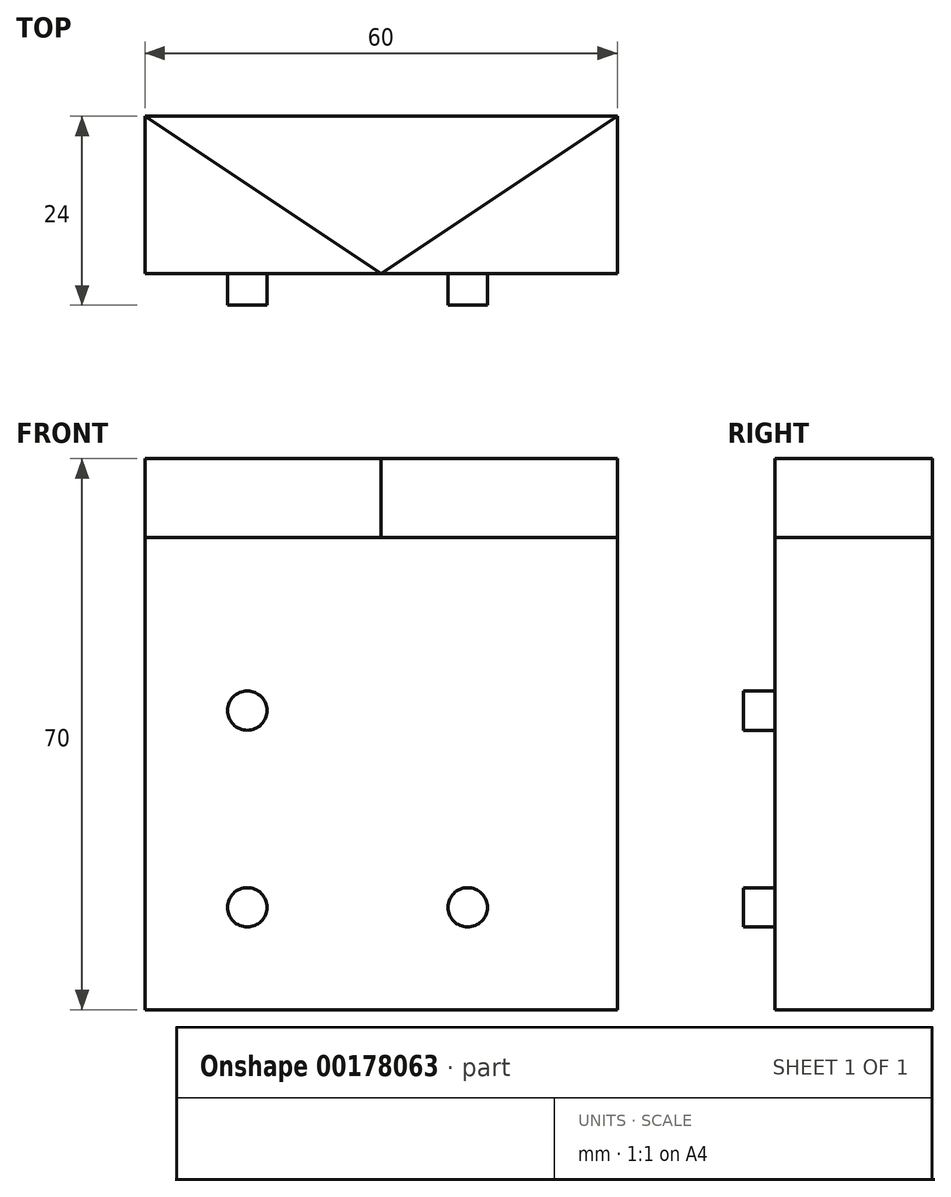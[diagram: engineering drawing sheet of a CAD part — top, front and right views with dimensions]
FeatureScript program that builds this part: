
annotation { "Feature Type Name" : "Feature", "Feature Type Description" : "" }
export const myFeature = defineFeature(function(context is Context, id is Id, definition is map)
    precondition{}
    {
        {
            var Q0;
            Q0=qCreatedBy(makeId("Right.planeOp"),FACE);
            var sketch = newSketch(context, id + "F0", { "sketchPlane" : qUnion([Q0])});
            skLineSegment(sketch, "E0.bottom", {"start": v(10, 30) * mm, "end": v(-10, 30) * mm});
            skLineSegment(sketch, "E0.top", {"start": v(10, -30) * mm, "end": v(-10, -30) * mm});
            skLineSegment(sketch, "E0.left", {"start": v(10, 30) * mm, "end": v(10, -30) * mm});
            skLineSegment(sketch, "E0.right", {"start": v(-10, 30) * mm, "end": v(-10, -30) * mm});
            skPoint(sketch, "E0.middle", {"position": v(0, 0) * mm});
            skSolve(sketch);
        }
        {
            var Q0;
            Q0 = qSketchRegion(id + "F0", true);
            extrude(context, id + "F1", {"entities" : qUnion([Q0]), "depth" : 30 * mm, "hasSecondDirection" : true, "secondDirectionOppositeDirection" : true, "secondDirectionDepth" : 30 * mm});
        }
        {
            var Q0;
            Q0=makeQuery(id+"F1.opExtrude","SWEPT_FACE",FACE,{"disambiguationData":[OSD([sQuery(id+"F0.wireOp",EDGE,"E0.bottom")])]});
            var sketch = newSketch(context, id + "F2", { "sketchPlane" : qUnion([Q0])});
            skLineSegment(sketch, "E1", {"start": v(-30, 10) * mm, "end": v(0, -10) * mm});
            skLineSegment(sketch, "E2", {"start": v(0, -10) * mm, "end": v(30, 10) * mm});
            skLineSegment(sketch, "E3", {"start": v(30, 10) * mm, "end": v(-30, 10) * mm});
            skSolve(sketch);
        }
        {
            var Q0;
            Q0 = qSketchRegion(id + "F2", true);
            extrude(context, id + "F3", {"entities" : qUnion([Q0]), "operationType" : NewBodyOperationType.ADD, "depth" : 10 * mm});
        }
        {
            var Q0;
            Q0=makeQuery(id+"F1.opExtrude","SWEPT_FACE",FACE,{"disambiguationData":[OSD([sQuery(id+"F0.wireOp",EDGE,"E0.right")])]});
            var sketch = newSketch(context, id + "F4", { "sketchPlane" : qUnion([Q0])});
            skCircle(sketch, "E4", {"center": v(-17, 8) * mm, "radius": 2.5 * mm});
            skCircle(sketch, "E5", {"center": v(-17, -17) * mm, "radius": 2.5 * mm});
            skCircle(sketch, "E6", {"center": v(11, -17) * mm, "radius": 2.5 * mm});
            skSolve(sketch);
        }
        {
            var Q0;
            Q0 = qSketchRegion(id + "F4", true);
            extrude(context, id + "F5", {"entities" : qUnion([Q0]), "operationType" : NewBodyOperationType.ADD, "depth" : 4 * mm});
        }
    });
